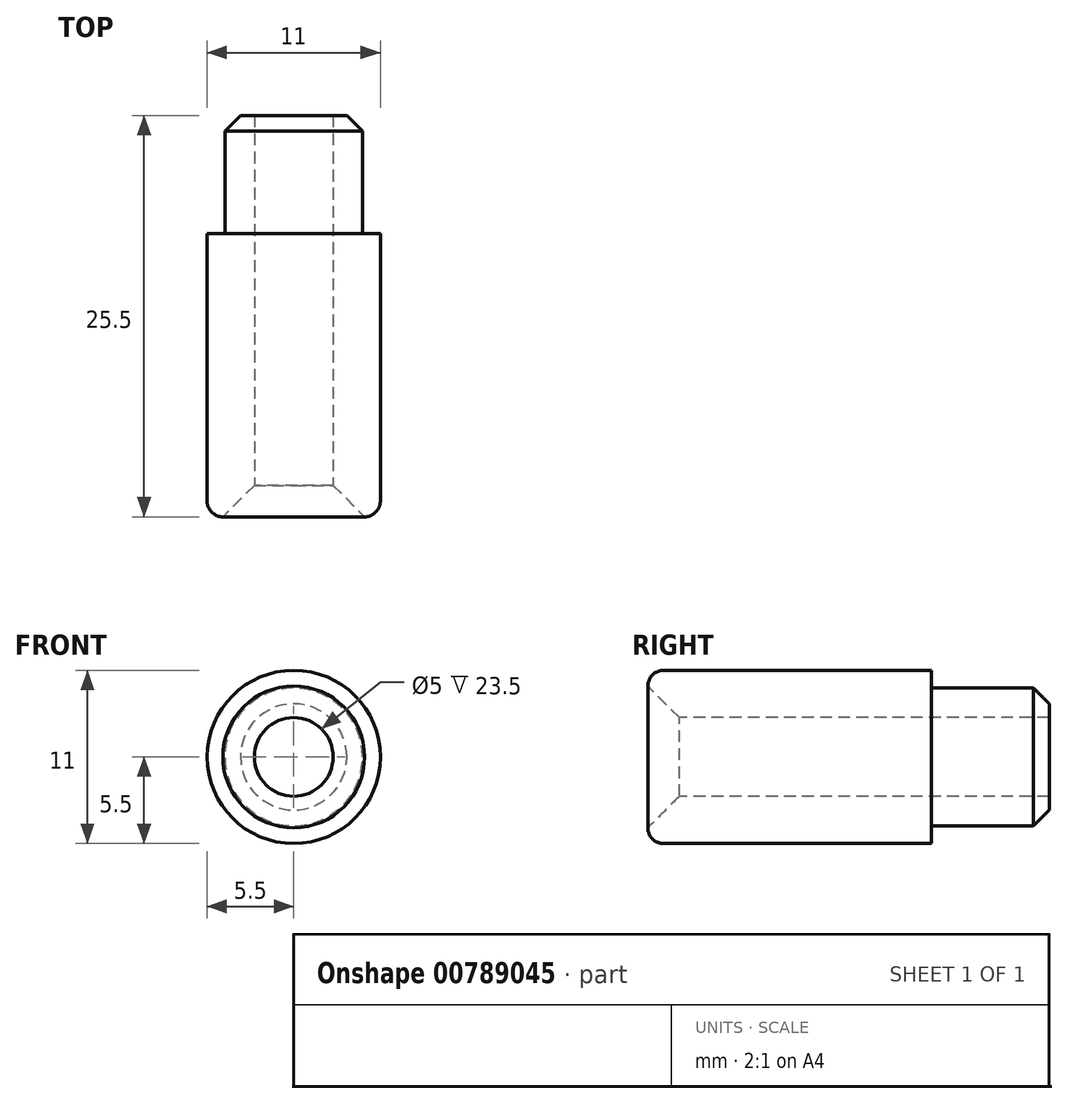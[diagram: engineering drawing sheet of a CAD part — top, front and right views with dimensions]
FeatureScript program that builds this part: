
annotation { "Feature Type Name" : "Feature", "Feature Type Description" : "" }
export const myFeature = defineFeature(function(context is Context, id is Id, definition is map)
    precondition{}
    {
        {
            var Q0;
            Q0=qCreatedBy(makeId("Front.planeOp"),FACE);
            var sketch = newSketch(context, id + "F0", { "sketchPlane" : qUnion([Q0])});
            skCircle(sketch, "E0", {"center": v(0, 0) * mm, "radius": 5.5 * mm});
            skSolve(sketch);
        }
        {
            var Q0;
            Q0 = qSketchRegion(id + "F0", true);
            extrude(context, id + "F1", {"entities" : qUnion([Q0]), "depth" : 18 * mm, "offsetDistance" : 25 * mm});
        }
        {
            var Q0;
            Q0=makeQuery(id+"F1.opExtrude","CAP_EDGE",EDGE,{"disambiguationData":[OSD([sQuery(id+"F0.wireOp",EDGE,"E0")])],"isStart":false});
            fillet(context, id + "F2", {"entities" : qUnion([Q0]), "radius" : 1 * mm, "tangentPropagation" : true, "allowEdgeOverflow" : false});
        }
        {
            var Q0;
            Q0=makeQuery(id+"F1.opExtrude","CAP_FACE",FACE,{"disambiguationData":[OSD([sQuery(id+"F0.wireOp",EDGE,"E0")])],"isStart":true});
            var sketch = newSketch(context, id + "F3", { "sketchPlane" : qUnion([Q0])});
            skCircle(sketch, "E1", {"center": v(0, 0) * mm, "radius": 4.38 * mm});
            skSolve(sketch);
        }
        {
            var Q0;
            Q0=makeQuery(id+"F3.imprint","IMPRINT",FACE,{"disambiguationData":[TD([[makeQuery(id+"F3.imprint","IMPRINT",EDGE,{"derivedFrom":sQuery(id+"F3.wireOp",EDGE,"E1")}),1.0]])]});
            extrude(context, id + "F4", {"entities" : qUnion([Q0]), "operationType" : NewBodyOperationType.ADD, "depth" : 7.5 * mm, "offsetDistance" : 25 * mm});
        }
        {
            var Q0;
            Q0=makeQuery(id+"F4.opExtrude","CAP_EDGE",EDGE,{"disambiguationData":[OSD([sQuery(id+"F3.wireOp",EDGE,"E1")])],"isStart":false});
            chamfer(context, id + "F5", {"entities" : qUnion([Q0]), "width" : 1 * mm, "tangentPropagation" : true});
        }
        {
            var Q0;
            Q0=makeQuery(id+"F1.opExtrude","CAP_FACE",FACE,{"disambiguationData":[OSD([sQuery(id+"F0.wireOp",EDGE,"E0")])],"isStart":false});
            var sketch = newSketch(context, id + "F6", { "sketchPlane" : qUnion([Q0])});
            skPoint(sketch, "E2", {"position": v(0, 0) * mm});
            skSolve(sketch);
        }
        {
            var Q0;
            Q0=sQuery(id+"F6.wireOp",VERTEX,"E2");
            var Q1;
            Q1=makeQuery(id+"F1.opExtrude","SWEPT_BODY",BODY,{"disambiguationData":[OSD([sQuery(id+"F0.wireOp",EDGE,"E0")])]});
            hole(context, id + "F7", {"style" : HoleStyle.C_SINK, "endStyle" : HoleEndStyle.THROUGH, "holeDiameter" : 5 * mm, "cSinkDiameter" : 9 * mm, "cSinkAngle" : 90 * degree, "majorDiameter" : 5 * mm, "isTappedThrough" : true, "tappedDepth" : 12 * mm, "tapClearance" : 3, "locations" : qUnion([Q0]), "scope" : qUnion([Q1])});
        }
    });
